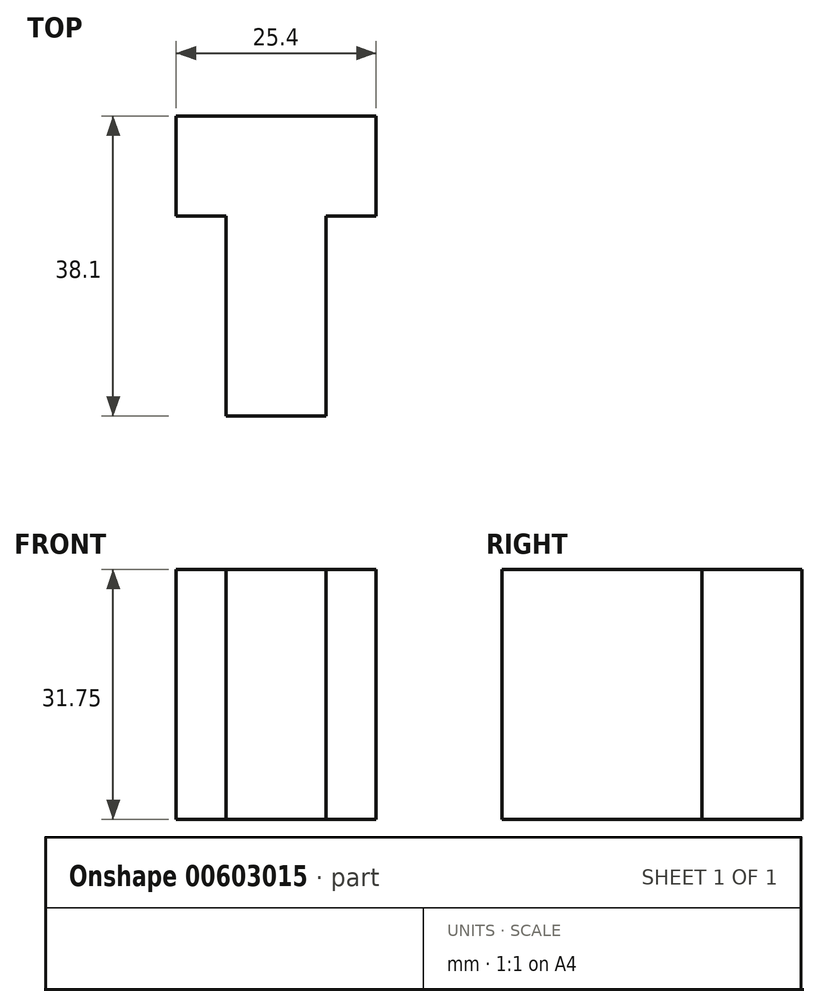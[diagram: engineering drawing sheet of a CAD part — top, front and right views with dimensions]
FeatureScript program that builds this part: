
annotation { "Feature Type Name" : "Feature", "Feature Type Description" : "" }
export const myFeature = defineFeature(function(context is Context, id is Id, definition is map)
    precondition{}
    {
        {
            var Q0;
            Q0=qCreatedBy(makeId("Top.planeOp"),FACE);
            var sketch = newSketch(context, id + "F0", { "sketchPlane" : qUnion([Q0])});
            skLineSegment(sketch, "E0", {"start": v(0, 0) * mm, "end": v(0, 25.4) * mm});
            skLineSegment(sketch, "E1", {"start": v(0, 25.4) * mm, "end": v(-6.35, 25.4) * mm});
            skLineSegment(sketch, "E2", {"start": v(-6.35, 25.4) * mm, "end": v(-6.35, 38.1) * mm});
            skLineSegment(sketch, "E3", {"start": v(-6.35, 38.1) * mm, "end": v(19.05, 38.1) * mm});
            skLineSegment(sketch, "E4", {"start": v(19.05, 38.1) * mm, "end": v(19.05, 25.4) * mm});
            skLineSegment(sketch, "E5", {"start": v(19.05, 25.4) * mm, "end": v(12.7, 25.4) * mm});
            skLineSegment(sketch, "E6", {"start": v(12.7, 25.4) * mm, "end": v(12.7, 0) * mm});
            skLineSegment(sketch, "E7", {"start": v(12.7, 0) * mm, "end": v(0, 0) * mm});
            skSolve(sketch);
        }
        {
            var Q0;
            Q0 = qSketchRegion(id + "F0", true);
            extrude(context, id + "F1", {"entities" : qUnion([Q0]), "depth" : 25.4 * mm, "offsetDistance" : 25.4 * mm});
        }
        {
            var Q0;
            Q0 = qSketchRegion(id + "F0", true);
            extrude(context, id + "F2", {"entities" : qUnion([Q0]), "operationType" : NewBodyOperationType.ADD, "depth" : 31.75 * mm, "offsetDistance" : 25.4 * mm});
        }
    });
